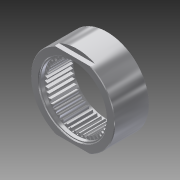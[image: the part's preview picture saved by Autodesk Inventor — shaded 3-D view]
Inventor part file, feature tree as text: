
AUTODESK INVENTOR PART (.ipt)
format: ipt  version: 2014 SP1 (Build 180222100, 222)  size: 420,864 bytes
history: native  units: in
note: dims shown in document units (in); Inventor stores cm internally (conversion verified against a paired STEP export)
features: extrude x4, sketch x3, chamfer x1, plane x1
ambient origin geometry x8: Origin, YZ Plane, XZ Plane, XY Plane, X Axis, Y Axis, Z Axis, Center Point
bodies: Solid1 (feature_tree)
feature tree (9):
  extrude  "Extrusion1"  Depth=1.175in
  chamfer  "Chamfer1"  Distance=0.6in
  extrude  "Extrusion2"  Depth=0.625in
  plane  "Work Plane1"
  sketch  "Sketch3"  dims[d8=0.0787in d9=0.0in d10=1.14in d12=0.5606in d13=0.0in d14=0.4425in d15=0.0in d16=1.45in]
  extrude  "Extrusion3"  Depth=0.4425in
  extrude  "Extrusion4"  Depth=0.5606in
  sketch  "Sketch1"  dims[d0=1.45in d1=1.175in d2=0.6in d3=0.0in]
  sketch  "Sketch2"  dims[d4=0.01in d5=0.125in d6=45.0deg d7=0.625in]
